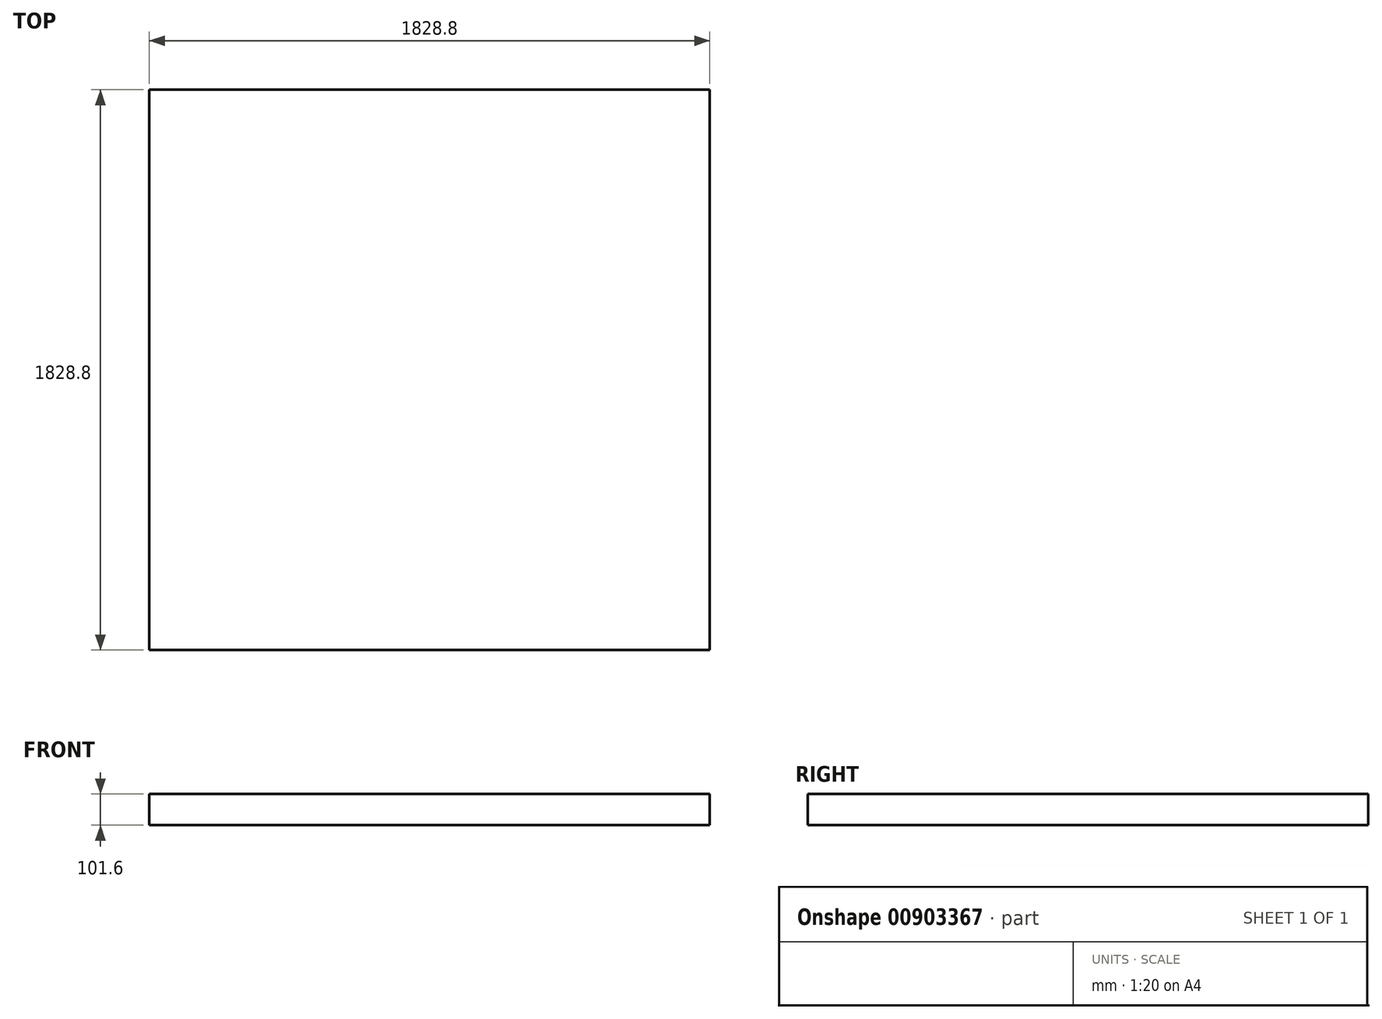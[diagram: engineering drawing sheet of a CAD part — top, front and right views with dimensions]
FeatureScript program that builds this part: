
annotation { "Feature Type Name" : "Feature", "Feature Type Description" : "" }
export const myFeature = defineFeature(function(context is Context, id is Id, definition is map)
    precondition{}
    {
        {
            var Q0;
            Q0=qCreatedBy(makeId("Top.planeOp"),FACE);
            var sketch = newSketch(context, id + "F0", { "sketchPlane" : qUnion([Q0])});
            skLineSegment(sketch, "E0.bottom", {"start": v(0, 0) * mm, "end": v(1828.8, 0) * mm});
            skLineSegment(sketch, "E0.top", {"start": v(0, 1828.8) * mm, "end": v(1828.8, 1828.8) * mm});
            skLineSegment(sketch, "E0.left", {"start": v(0, 0) * mm, "end": v(0, 1828.8) * mm});
            skLineSegment(sketch, "E0.right", {"start": v(1828.8, 0) * mm, "end": v(1828.8, 1828.8) * mm});
            skSolve(sketch);
        }
        {
            var Q0;
            Q0=makeQuery(id+"F0.imprint","IMPRINT",FACE,{"disambiguationData":[TD([[makeQuery(id+"F0.imprint","IMPRINT",EDGE,{"derivedFrom":sQuery(id+"F0.wireOp",EDGE,"E0.bottom")}),1.0]])]});
            extrude(context, id + "F1", {"entities" : qUnion([Q0]), "depth" : 101.6 * mm, "offsetDistance" : 25.4 * mm});
        }
    });
